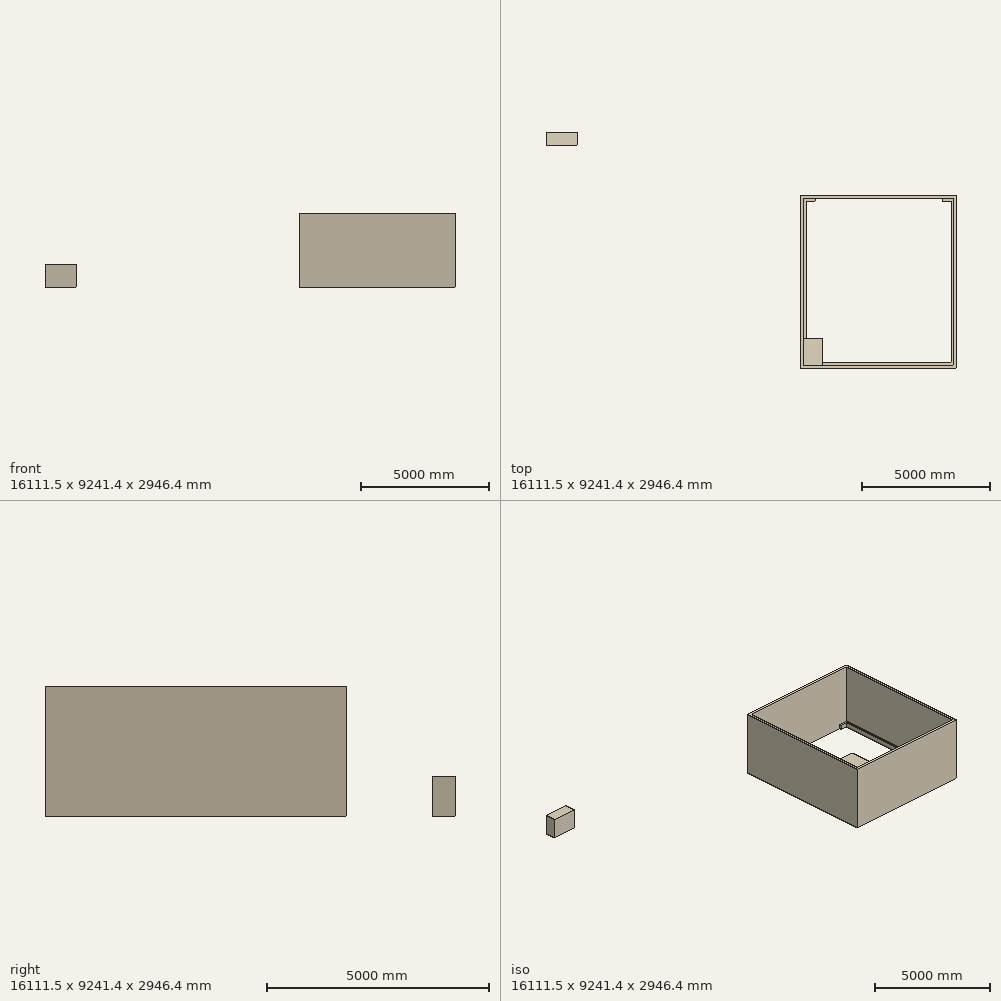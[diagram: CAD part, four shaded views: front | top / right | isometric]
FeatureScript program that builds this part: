
annotation { "Feature Type Name" : "Feature", "Feature Type Description" : "" }
export const myFeature = defineFeature(function(context is Context, id is Id, definition is map)
    precondition{}
    {
        {
            var Q0;
            Q0=qCreatedBy(makeId("Top.planeOp"),FACE);
            var sketch = newSketch(context, id + "F0", { "sketchPlane" : qUnion([Q0])});
            skLineSegment(sketch, "E0.bottom", {"start": v(-2945.27, 4089.53) * mm, "end": v(2947.53, 4089.53) * mm});
            skLineSegment(sketch, "E0.top", {"start": v(-2945.27, -2463.67) * mm, "end": v(2947.53, -2463.67) * mm});
            skLineSegment(sketch, "E0.left", {"start": v(-2945.27, 4089.53) * mm, "end": v(-2945.27, -2463.67) * mm});
            skLineSegment(sketch, "E0.right", {"start": v(2947.53, 4089.53) * mm, "end": v(2947.53, -2463.67) * mm});
            skSolve(sketch);
        }
        {
            var Q0;
            Q0=makeQuery(id+"F0.imprint","IMPRINT",FACE,{"disambiguationData":[TD([[makeQuery(id+"F0.imprint","IMPRINT",EDGE,{"derivedFrom":sQuery(id+"F0.wireOp",EDGE,"E0.bottom")}),-1.0]])]});
            var sketch = newSketch(context, id + "F1", { "sketchPlane" : qUnion([Q0])});
            skLineSegment(sketch, "E1.0", {"start": v(2845.93, 3987.93) * mm, "end": v(2845.93, -2362.07) * mm});
            skLineSegment(sketch, "E2.0", {"start": v(-2843.67, 3987.93) * mm, "end": v(-2488.07, 3987.93) * mm});
            skLineSegment(sketch, "E3.0", {"start": v(-2843.67, 3987.93) * mm, "end": v(-2843.67, -2362.07) * mm});
            skLineSegment(sketch, "E4.0", {"start": v(-2843.67, -2362.07) * mm, "end": v(2845.93, -2362.07) * mm});
            skLineSegment(sketch, "E5.0", {"start": v(-2488.07, 4089.53) * mm, "end": v(-2488.07, 3987.93) * mm});
            skLineSegment(sketch, "E6.0", {"start": v(2515.73, 4089.53) * mm, "end": v(2515.73, 3987.93) * mm});
            skLineSegment(sketch, "E7.trimOffspring", {"start": v(2515.73, 3987.93) * mm, "end": v(2845.93, 3987.93) * mm});
            skSolve(sketch);
        }
        {
            var Q0;
            Q0=makeQuery(id+"F1.imprint","IMPRINT",FACE,{"disambiguationData":[TD([[makeQuery(id+"F1.imprint","IMPRINT",EDGE,{"derivedFrom":sQuery(id+"F1.wireOp",EDGE,"E1.0")}),1.0]])]});
            extrude(context, id + "F2", {"entities" : qUnion([Q0]), "depth" : 203.2 * mm});
        }
        {
            var Q0;
            Q0=makeQuery(id+"F0.imprint","IMPRINT",FACE,{"disambiguationData":[TD([[makeQuery(id+"F0.imprint","IMPRINT",EDGE,{"derivedFrom":sQuery(id+"F0.wireOp",EDGE,"E0.bottom")}),-1.0]])]});
            var sketch = newSketch(context, id + "F3", { "sketchPlane" : qUnion([Q0])});
            skLineSegment(sketch, "E8.0", {"start": v(-3059.57, 4203.83) * mm, "end": v(-3059.57, -2577.97) * mm});
            skLineSegment(sketch, "E9.0", {"start": v(-3059.57, -2577.97) * mm, "end": v(3061.83, -2577.97) * mm});
            skLineSegment(sketch, "E10.0", {"start": v(3061.83, 4203.83) * mm, "end": v(3061.83, -2577.97) * mm});
            skLineSegment(sketch, "E11.0", {"start": v(-3059.57, 4203.83) * mm, "end": v(3061.83, 4203.83) * mm});
            skSolve(sketch);
        }
        {
            var Q0;
            Q0=makeQuery(id+"F3.imprint","IMPRINT",FACE,{"disambiguationData":[TD([[makeQuery(id+"F3.imprint","IMPRINT",EDGE,{"derivedFrom":sQuery(id+"F3.wireOp",EDGE,"E8.0")}),1.0]])]});
            var sketch = newSketch(context, id + "F4", { "sketchPlane" : qUnion([Q0])});
            skSolve(sketch);
        }
        {
            var Q0;
            Q0=makeQuery(id+"F4.imprint","IMPRINT",FACE,{"disambiguationData":[TD([[makeQuery(id+"F4.imprint","IMPRINT",EDGE,{"derivedFrom":makeQuery(id+"F3.imprint","IMPRINT",EDGE,{"derivedFrom":sQuery(id+"F3.wireOp",EDGE,"E8.0")})}),1.0]])]});
            extrude(context, id + "F5", {"entities" : qUnion([Q0]), "operationType" : NewBodyOperationType.ADD, "depth" : 2946.4 * mm});
        }
        {
            var Q0;
            Q0=makeQuery(id+"F0.imprint","IMPRINT",FACE,{"disambiguationData":[TD([[makeQuery(id+"F0.imprint","IMPRINT",EDGE,{"derivedFrom":sQuery(id+"F0.wireOp",EDGE,"E0.bottom")}),-1.0]])]});
            var sketch = newSketch(context, id + "F6", { "sketchPlane" : qUnion([Q0])});
            skLineSegment(sketch, "E12.0", {"start": v(-2945.27, -1422.27) * mm, "end": v(-2208.67, -1422.27) * mm});
            skLineSegment(sketch, "E13.0", {"start": v(-2208.67, -1422.27) * mm, "end": v(-2208.67, -2463.67) * mm});
            skLineSegment(sketch, "E14", {"start": v(-2945.27, -1422.27) * mm, "end": v(-2945.27, -2463.67) * mm});
            skLineSegment(sketch, "E15", {"start": v(-2945.27, -2463.67) * mm, "end": v(-2208.67, -2463.67) * mm});
            skLineSegment(sketch, "E16", {"start": v(-2208.67, -2463.67) * mm, "end": v(-2208.67, -1422.27) * mm});
            skSolve(sketch);
        }
        {
            var Q0;
            Q0=makeQuery(id+"F6.imprint","IMPRINT",FACE,{"disambiguationData":[TD([[makeQuery(id+"F6.imprint","IMPRINT",EDGE,{"derivedFrom":sQuery(id+"F6.wireOp",EDGE,"E14")}),1.0]])]});
            extrude(context, id + "F7", {"entities" : qUnion([Q0]), "depth" : 2946.4 * mm});
        }
        {
            var Q0;
            Q0=makeQuery(id+"F3.imprint","IMPRINT",FACE,{"disambiguationData":[TD([[makeQuery(id+"F3.imprint","IMPRINT",EDGE,{"derivedFrom":makeQuery(id+"F0.imprint","IMPRINT",EDGE,{"derivedFrom":sQuery(id+"F0.wireOp",EDGE,"E0.bottom")})}),-1.0]])]});
            var sketch = newSketch(context, id + "F8", { "sketchPlane" : qUnion([Q0])});
            skLineSegment(sketch, "E17.bottom", {"start": v(-13049.7, 6663.47) * mm, "end": v(-11830.5, 6663.47) * mm});
            skLineSegment(sketch, "E17.top", {"start": v(-13049.7, 6155.47) * mm, "end": v(-11830.5, 6155.47) * mm});
            skLineSegment(sketch, "E17.left", {"start": v(-13049.7, 6663.47) * mm, "end": v(-13049.7, 6155.47) * mm});
            skLineSegment(sketch, "E17.right", {"start": v(-11830.5, 6663.47) * mm, "end": v(-11830.5, 6155.47) * mm});
            skText(sketch, "E18", { "text": "Jointer", "fontName": "OpenSans-Regular.ttf"});
            const initialGuessF8  = {"E18": [-12.98214, 6.31163, 1, 0, 0.25586]};
            skSetInitialGuess(sketch, initialGuessF8);
            skSolve(sketch);
        }
        {
            var Q0;
            Q0=makeQuery(id+"F8.imprint","IMPRINT",FACE,{"disambiguationData":[TD([[makeQuery(id+"F8.imprint","IMPRINT",EDGE,{"derivedFrom":sQuery(id+"F8.wireOp",EDGE,"E18.sketch_text.stroke-94")}),-1.0]])]});
            var Q1;
            Q1=makeQuery(id+"F8.imprint","IMPRINT",FACE,{"disambiguationData":[TD([[makeQuery(id+"F8.imprint","IMPRINT",EDGE,{"derivedFrom":sQuery(id+"F8.wireOp",EDGE,"E18.sketch_text.stroke-89")}),1.0]])]});
            var Q2;
            Q2=makeQuery(id+"F8.imprint","IMPRINT",FACE,{"disambiguationData":[TD([[makeQuery(id+"F8.imprint","IMPRINT",EDGE,{"derivedFrom":sQuery(id+"F8.wireOp",EDGE,"E18.sketch_text.stroke-75")}),-1.0]])]});
            var Q3;
            Q3=makeQuery(id+"F8.imprint","IMPRINT",FACE,{"disambiguationData":[TD([[makeQuery(id+"F8.imprint","IMPRINT",EDGE,{"derivedFrom":sQuery(id+"F8.wireOp",EDGE,"E18.sketch_text.stroke-39")}),-1.0]])]});
            var Q4;
            Q4=makeQuery(id+"F8.imprint","IMPRINT",FACE,{"disambiguationData":[TD([[makeQuery(id+"F8.imprint","IMPRINT",EDGE,{"derivedFrom":sQuery(id+"F8.wireOp",EDGE,"E18.sketch_text.stroke-56")}),-1.0]])]});
            var Q5;
            Q5=makeQuery(id+"F8.imprint","IMPRINT",FACE,{"disambiguationData":[TD([[makeQuery(id+"F8.imprint","IMPRINT",EDGE,{"derivedFrom":sQuery(id+"F8.wireOp",EDGE,"E18.sketch_text.stroke-19")}),1.0]])]});
            var Q6;
            Q6=makeQuery(id+"F8.imprint","IMPRINT",FACE,{"disambiguationData":[TD([[makeQuery(id+"F8.imprint","IMPRINT",EDGE,{"derivedFrom":sQuery(id+"F8.wireOp",EDGE,"E17.bottom")}),-1.0]])]});
            var Q7;
            Q7=makeQuery(id+"F8.imprint","IMPRINT",FACE,{"disambiguationData":[TD([[makeQuery(id+"F8.imprint","IMPRINT",EDGE,{"derivedFrom":sQuery(id+"F8.wireOp",EDGE,"E18.sketch_text.stroke-27")}),-1.0]])]});
            var Q8;
            Q8=makeQuery(id+"F8.imprint","IMPRINT",FACE,{"disambiguationData":[TD([[makeQuery(id+"F8.imprint","IMPRINT",EDGE,{"derivedFrom":sQuery(id+"F8.wireOp",EDGE,"E18.sketch_text.stroke-0")}),-1.0]])]});
            var Q9;
            Q9=makeQuery(id+"F8.imprint","IMPRINT",FACE,{"disambiguationData":[TD([[makeQuery(id+"F8.imprint","IMPRINT",EDGE,{"derivedFrom":sQuery(id+"F8.wireOp",EDGE,"E18.sketch_text.stroke-10")}),-1.0]])]});
            var Q10;
            Q10=makeQuery(id+"F8.imprint","IMPRINT",FACE,{"disambiguationData":[TD([[makeQuery(id+"F8.imprint","IMPRINT",EDGE,{"derivedFrom":sQuery(id+"F8.wireOp",EDGE,"E18.sketch_text.stroke-31")}),-1.0]])]});
            extrude(context, id + "F9", {"entities" : qUnion([Q0, Q1, Q2, Q3, Q4, Q5, Q6, Q7, Q8, Q9, Q10]), "depth" : 914.4 * mm});
        }
    });
